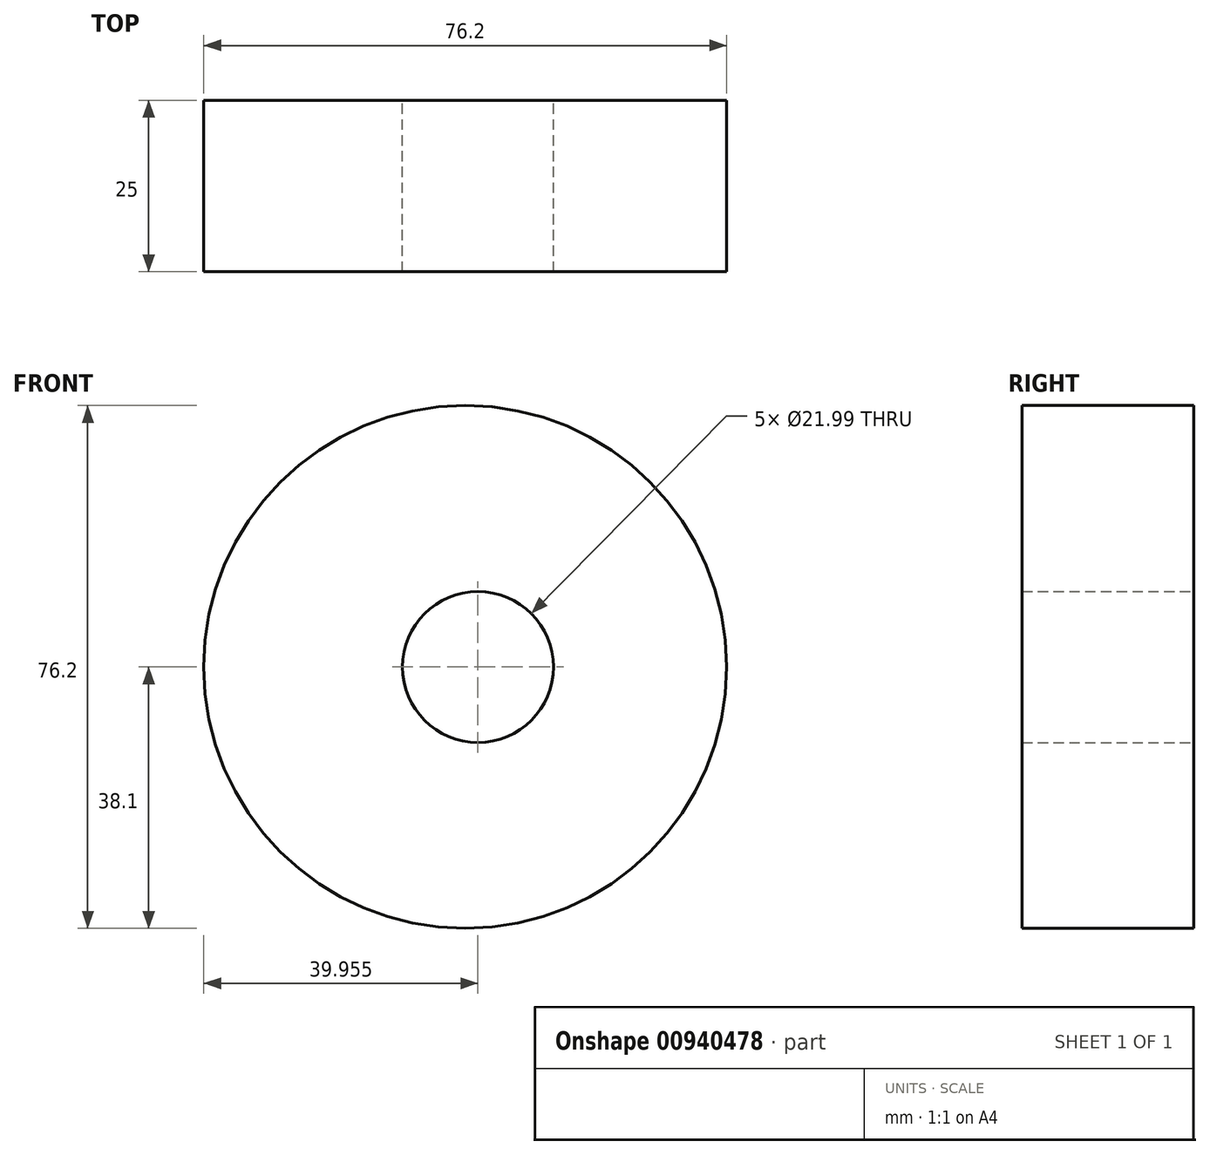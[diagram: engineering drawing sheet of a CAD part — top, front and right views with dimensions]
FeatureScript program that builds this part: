
annotation { "Feature Type Name" : "Feature", "Feature Type Description" : "" }
export const myFeature = defineFeature(function(context is Context, id is Id, definition is map)
    precondition{}
    {
        {
            var Q0;
            Q0=qCreatedBy(makeId("Front.planeOp"),FACE);
            var sketch = newSketch(context, id + "F0", { "sketchPlane" : qUnion([Q0])});
            skCircle(sketch, "E0", {"center": v(0, 0) * mm, "radius": 38.1 * mm});
            skCircle(sketch, "E1", {"center": v(1.85, 0) * mm, "radius": 11 * mm});
            skSolve(sketch);
        }
        {
            var Q0;
            Q0 = qSketchRegion(id + "F0", true);
            extrude(context, id + "F1", {"entities" : qUnion([Q0]), "depth" : 25 * mm, "offsetDistance" : 25 * mm});
        }
    });
